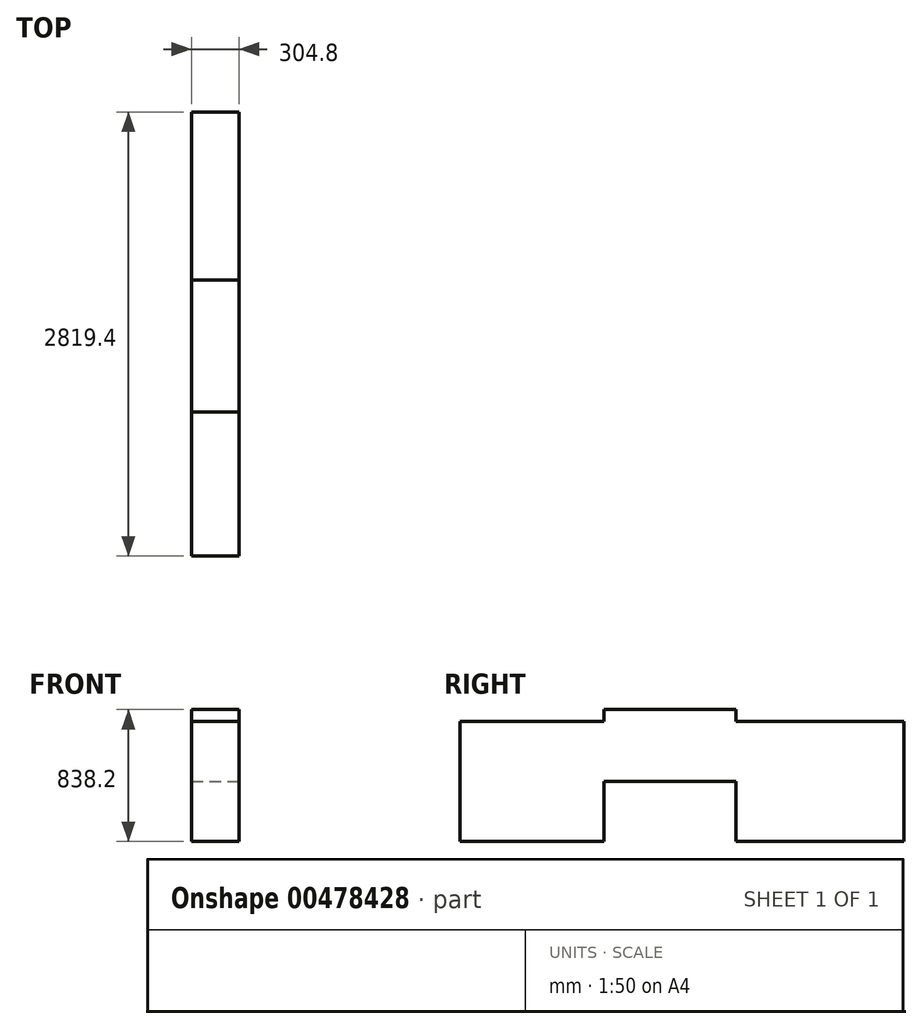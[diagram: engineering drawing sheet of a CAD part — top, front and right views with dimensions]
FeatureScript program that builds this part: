
annotation { "Feature Type Name" : "Feature", "Feature Type Description" : "" }
export const myFeature = defineFeature(function(context is Context, id is Id, definition is map)
    precondition{}
    {
        {
            var Q0;
            Q0=qCreatedBy(makeId("Right.planeOp"),FACE);
            var sketch = newSketch(context, id + "F0", { "sketchPlane" : qUnion([Q0])});
            skLineSegment(sketch, "E0.bottom", {"start": v(-1409.7, -381) * mm, "end": v(1409.7, -381) * mm});
            skLineSegment(sketch, "E0.top", {"start": v(-1409.7, 381) * mm, "end": v(1409.7, 381) * mm});
            skLineSegment(sketch, "E0.left", {"start": v(-1409.7, -381) * mm, "end": v(-1409.7, 381) * mm});
            skLineSegment(sketch, "E0.right", {"start": v(1409.7, -381) * mm, "end": v(1409.7, 381) * mm});
            skSolve(sketch);
        }
        {
            var Q0;
            Q0 = qSketchRegion(id + "F0", true);
            var Q1;
            Q1=makeQuery(id+"F0.imprint","IMPRINT",FACE,{"disambiguationData":[TD([[makeQuery(id+"F0.imprint","IMPRINT",EDGE,{"derivedFrom":sQuery(id+"F0.wireOp",EDGE,"E0.bottom")}),1.0]])]});
            extrude(context, id + "F1", {"entities" : qUnion([Q0, Q1]), "depth" : 304.8 * mm});
        }
        {
            var Q0;
            Q0=makeQuery(id+"F1.opExtrude","CAP_FACE",FACE,{"disambiguationData":[OSD([sQuery(id+"F0.wireOp",EDGE,"E0.bottom"),sQuery(id+"F0.wireOp",EDGE,"E0.top"),sQuery(id+"F0.wireOp",EDGE,"E0.left"),sQuery(id+"F0.wireOp",EDGE,"E0.right")])],"isStart":false});
            var sketch = newSketch(context, id + "F2", { "sketchPlane" : qUnion([Q0])});
            skLineSegment(sketch, "E1.bottom", {"start": v(-495.3, 0) * mm, "end": v(342.9, 0) * mm});
            skLineSegment(sketch, "E1.top", {"start": v(-495.3, -381) * mm, "end": v(342.9, -381) * mm});
            skLineSegment(sketch, "E1.left", {"start": v(-495.3, 0) * mm, "end": v(-495.3, -381) * mm});
            skLineSegment(sketch, "E1.right", {"start": v(342.9, 0) * mm, "end": v(342.9, -381) * mm});
            skSolve(sketch);
        }
        {
            var Q0;
            Q0=makeQuery(id+"F2.imprint","IMPRINT",FACE,{"disambiguationData":[TD([[makeQuery(id+"F2.imprint","IMPRINT",EDGE,{"derivedFrom":sQuery(id+"F2.wireOp",EDGE,"E1.bottom")}),-1.0]])]});
            extrude(context, id + "F3", {"entities" : qUnion([Q0]), "operationType" : NewBodyOperationType.REMOVE, "oppositeDirection" : true, "depth" : 304.8 * mm});
        }
        {
            var Q0;
            Q0=makeQuery(id+"F1.opExtrude","SWEPT_FACE",FACE,{"disambiguationData":[OSD([sQuery(id+"F0.wireOp",EDGE,"E0.top")])]});
            var sketch = newSketch(context, id + "F4", { "sketchPlane" : qUnion([Q0])});
            skLineSegment(sketch, "E2.bottom", {"start": v(304.8, 342.9) * mm, "end": v(0, 342.9) * mm});
            skLineSegment(sketch, "E2.top", {"start": v(304.8, -495.3) * mm, "end": v(0, -495.3) * mm});
            skLineSegment(sketch, "E2.left", {"start": v(304.8, 342.9) * mm, "end": v(304.8, -495.3) * mm});
            skLineSegment(sketch, "E2.right", {"start": v(0, 342.9) * mm, "end": v(0, -495.3) * mm});
            skSolve(sketch);
        }
        {
            var Q0;
            Q0=makeQuery(id+"F4.imprint","IMPRINT",FACE,{"disambiguationData":[TD([[makeQuery(id+"F4.imprint","IMPRINT",EDGE,{"derivedFrom":sQuery(id+"F4.wireOp",EDGE,"E2.bottom")}),1.0]])]});
            extrude(context, id + "F5", {"entities" : qUnion([Q0]), "operationType" : NewBodyOperationType.ADD, "depth" : 76.2 * mm});
        }
    });
